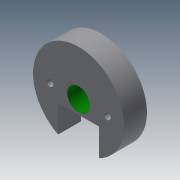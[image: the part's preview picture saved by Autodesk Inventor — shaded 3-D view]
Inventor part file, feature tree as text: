
AUTODESK INVENTOR PART (.ipt)
format: ipt  version: 2013 (Build 170138000, 138)  size: 124,928 bytes
history: native  units: mm
features: sketch x9, extrude x7
ambient origin geometry x8: Origin, YZ Plane, XZ Plane, XY Plane, X Axis, Y Axis, Z Axis, Center Point
bodies: Solid1 (feature_tree)
feature tree (16):
  extrude  "Extrusion1"  Depth=10.0mm TaperAngle=0.0deg
  extrude  "Extrusion2"  Depth=10.0mm TaperAngle=0.0deg
  extrude  "Extrusion3"  Depth=3.0mm
  sketch  "Sketch4"  dims[d9=10.0mm d10=0.0mm d11=10.0mm]
  sketch  "Sketch5"  dims[d12=10.0mm d13=0.0mm d14=6.0mm]
  extrude  "Extrusion4"  Depth=10.0mm
  extrude  "Extrusion5"  Depth=6.0mm
  extrude  "Extrusion6"  Depth=18.0mm
  extrude  "Extrusion7"  Depth=10.0mm TaperAngle=0.0deg
  sketch  "Sketch1"  dims[d0=40.0mm d1=10.0mm d2=0.0mm]
  sketch  "Sketch2"  dims[d3=12.0mm d4=10.0mm d5=0.0mm]
  sketch  "Sketch3"  dims[d7=3.0mm d8=3.0mm]
  sketch  "Sketch6"  dims[d15=2.0mm d16=0.0mm d17=18.0mm]
  sketch  "Sketch7"  dims[d18=10.0mm d19=10.0mm d20=0.0mm]
  sketch  "Sketch8"  dims[d21=18.0mm]
  sketch  "Sketch9"  dims[d25=2.0mm d26=10.0mm d27=0.0mm]
